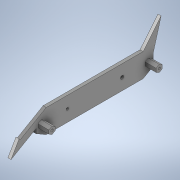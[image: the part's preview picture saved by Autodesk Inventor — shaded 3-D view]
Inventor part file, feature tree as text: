
AUTODESK INVENTOR PART (.ipt)
format: ipt  version: 2020 (Build 240168000, 168)  size: 183,296 bytes
history: native  units: in
note: dims shown in document units (in); Inventor stores cm internally (conversion verified against a paired STEP export)
features: other x3, extrude x2, sketch x2
ambient origin geometry x8: Origin, YZ Plane, XZ Plane, XY Plane, X Axis, Y Axis, Z Axis, Center Point
bodies: Solid1 (feature_tree)
feature tree (7):
  other  "HexWheelGuard.ipt"
  extrude  "Extrusion1"  TaperAngle=0.0deg  [1 undecoded]
  extrude  "Extrusion2"  Depth=0.3937in
  other  "Solid1::HexWheelGuard.ipt"
  other  "TaggingFeature1"
  sketch  "Sketch1"  dims[d0=0.3937in d6=0.0in d7=0.0in]
  sketch  "Sketch2"  dims[d9=0.315in d10=1.3858in d11=60.0deg d12=0.0787in d13=0.3937in d14=0.0in d20=0.3937in d21=0.3937in d22=1.1024in]
note: 1 required parameter value undecoded (feature->parameter linkage not recoverable at this tier; creation-order binding heuristic only, values carry confidence <= 0.55)
